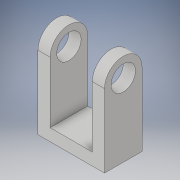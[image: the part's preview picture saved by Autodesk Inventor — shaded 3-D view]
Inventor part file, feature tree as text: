
AUTODESK INVENTOR PART (.ipt)
format: ipt  version: 2017 (Build 210142000, 142)  size: 119,808 bytes
history: native  units: in
note: dims shown in document units (in); Inventor stores cm internally (conversion verified against a paired STEP export)
features: extrude x2, sketch x2
ambient origin geometry x8: Origin, YZ Plane, XZ Plane, XY Plane, X Axis, Y Axis, Z Axis, Center Point
bodies: Solid1 (feature_tree)
feature tree (4):
  extrude  "Extrusion1"  Depth=0.77in
  extrude  "Extrusion2"  Depth=0.77in
  sketch  "Sketch1"  dims[d0=0.5in d1=0.77in]
  sketch  "Sketch2"  dims[d2=1.5in d3=0.77in d4=1.365in d5=0.0in d7=1.635in d8=0.25in d9=0.25in d10=1.26in d11=0.0in d12=0.25in]
